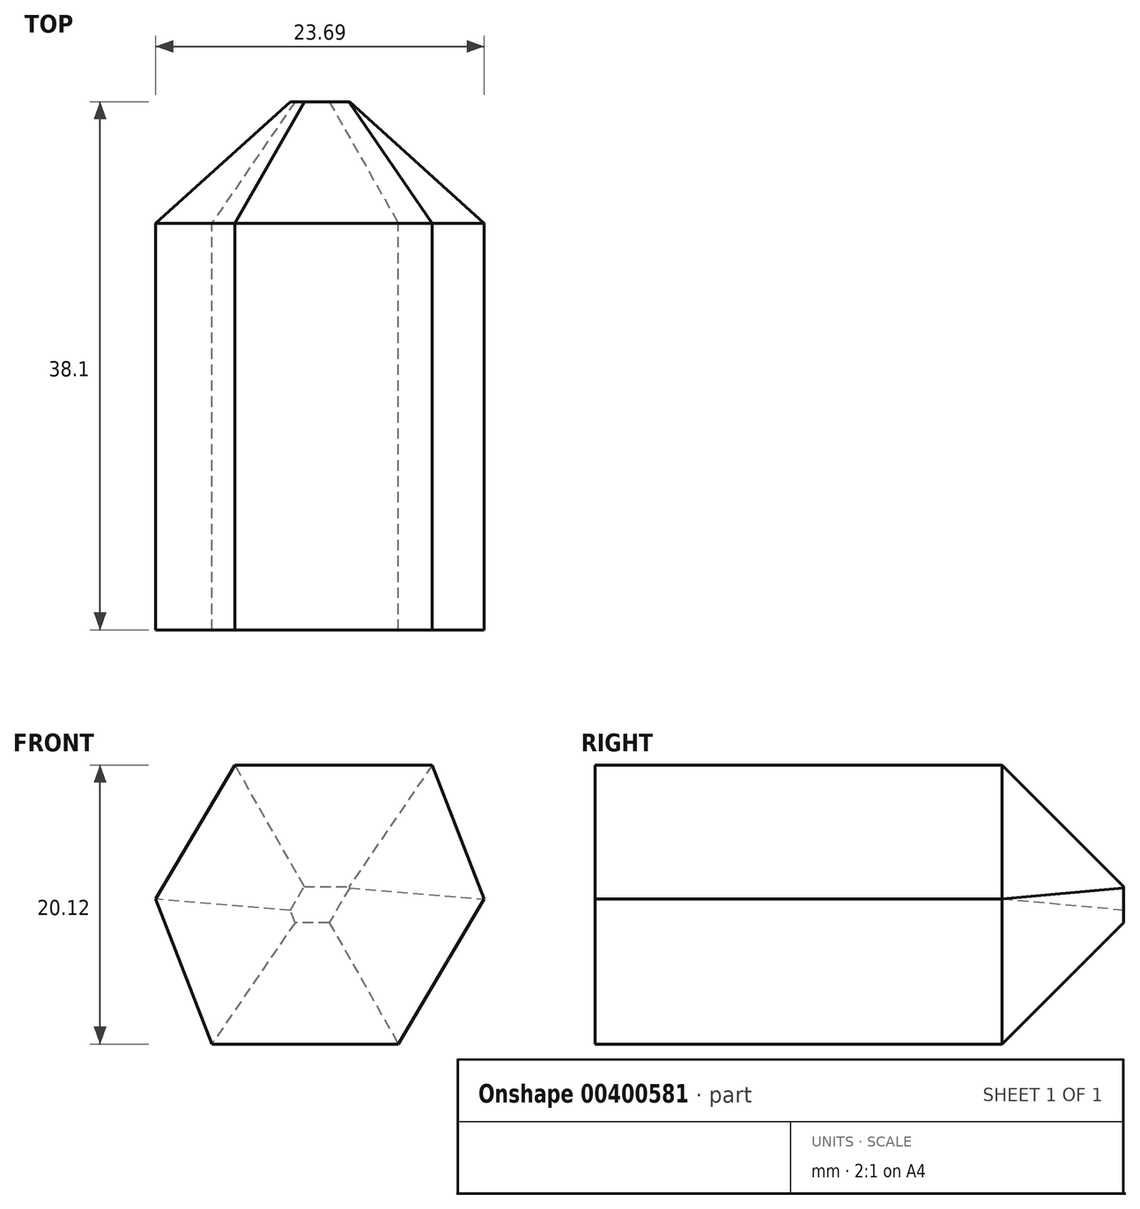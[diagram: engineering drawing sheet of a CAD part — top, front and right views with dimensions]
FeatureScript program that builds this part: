
annotation { "Feature Type Name" : "Feature", "Feature Type Description" : "" }
export const myFeature = defineFeature(function(context is Context, id is Id, definition is map)
    precondition{}
    {
        {
            var Q0;
            Q0=qCreatedBy(makeId("Front.planeOp"),FACE);
            var sketch = newSketch(context, id + "F0", { "sketchPlane" : qUnion([Q0])});
            skLineSegment(sketch, "E0", {"start": v(-12.7, 0) * mm, "end": v(-6.98, 9.67) * mm});
            skLineSegment(sketch, "E1", {"start": v(-6.98, 9.67) * mm, "end": v(7.24, 9.67) * mm});
            skLineSegment(sketch, "E2", {"start": v(7.24, 9.67) * mm, "end": v(10.99, 0) * mm});
            skLineSegment(sketch, "E3", {"start": v(10.99, 0) * mm, "end": v(4.8, -10.45) * mm});
            skLineSegment(sketch, "E4", {"start": v(4.8, -10.45) * mm, "end": v(-8.65, -10.45) * mm});
            skLineSegment(sketch, "E5", {"start": v(-8.65, -10.45) * mm, "end": v(-12.7, 0) * mm});
            skPoint(sketch, "E6", {"position": v(0, 0) * mm});
            skSolve(sketch);
        }
        {
            var Q0;
            Q0=makeQuery(id+"F0.imprint","IMPRINT",FACE,{"disambiguationData":[TD([[makeQuery(id+"F0.imprint","IMPRINT",EDGE,{"derivedFrom":sQuery(id+"F0.wireOp",EDGE,"E0")}),-1.0]])]});
            extrude(context, id + "F1", {"entities" : qUnion([Q0]), "depth" : 38.1 * mm});
        }
        {
            var Q0;
            Q0=makeQuery(id+"F1.opExtrude","CAP_FACE",FACE,{"disambiguationData":[OSD([sQuery(id+"F0.wireOp",EDGE,"E0"),sQuery(id+"F0.wireOp",EDGE,"E1"),sQuery(id+"F0.wireOp",EDGE,"E2"),sQuery(id+"F0.wireOp",EDGE,"E3"),sQuery(id+"F0.wireOp",EDGE,"E4"),sQuery(id+"F0.wireOp",EDGE,"E5")])],"isStart":true});
            chamfer(context, id + "F2", {"entities" : qUnion([Q0]), "width" : 8.76 * mm, "tangentPropagation" : true});
        }
    });
